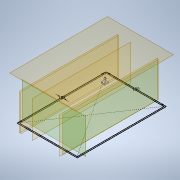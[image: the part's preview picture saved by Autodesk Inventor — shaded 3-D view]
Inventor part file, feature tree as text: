
AUTODESK INVENTOR PART (.ipt)
format: ipt  version: 2021 (Build 250183000, 183)  size: 425,984 bytes
history: native  units: in
note: dims shown in document units (in); Inventor stores cm internally (conversion verified against a paired STEP export)
features: sketch x26, extrude x20, reference x16, plane x7, mirror x4, other x4, revolve x2, chamfer x1, fillet x1
ambient origin geometry x8: Origin, YZ Plane, XZ Plane, XY Plane, X Axis, Y Axis, Z Axis, Center Point
bodies: Solid1 (feature_tree)
feature tree (81):
  sketch  "Sketch1"  dims[d0=3.937in d1=5.9055in]
  extrude  "Extrusion1"  Depth=5.9055in
  extrude  "Extrusion2"  Depth=0.0787in TaperAngle=0.0deg
  sketch  "Sketch2"  dims[d5=0.0787in d6=0.0in d7=-1.5748in]
  plane  "Work Plane1"
  extrude  "Extrusion3"  [1 undecoded]
  sketch  "Sketch7"  dims[d19=0.1181in d20=0.0in d21=2.8346in]
  plane  "Work Plane2"
  revolve  "Revolution2"  [1 undecoded]
  plane  "Work Plane3"
  extrude  "Extrusion4"  Depth=0.7087in
  sketch  "Sketch Driven Pattern1"  dims[d2=0.0787in d3=2.1654in d4=0.0in]
  extrude  "Extrusion5"  Depth=2.8346in
  plane  "Work Plane4"
  extrude  "Extrusion6"  Depth=0.1102in
  extrude  "Extrusion7"  Depth=0.1339in
  extrude  "Extrusion8"  TaperAngle=90.0deg  [1 undecoded]
  mirror  "Mirror1"
  plane  "Work Plane5"
  extrude  "Extrusion9"  Depth=0.0118in
  extrude  "Extrusion10"  Depth=0.0299in
  extrude  "Extrusion11"  Depth=0.0787in
  chamfer  "Chamfer1"  Distance=0.0787in
  extrude  "Extrusion12"  Depth=1.1811in
  sketch  "Sketch22"  dims[d47=0.5933in d48=0.0in d49=0.0866in]
  plane  "Work Plane6"
  revolve  "Revolution3"  [1 undecoded]
  extrude  "Extrusion13"  Depth=0.3819in
  sketch  "Sketch Driven Pattern2"  dims[d15=1.378in d16=1.2598in]
  extrude  "Extrusion14"  Depth=0.0866in
  extrude  "Extrusion15"  Depth=0.3236in
  extrude  "Extrusion16"  Depth=0.4724in
  plane  "Work Plane7"
  mirror  "Mirror2"
  extrude  "Extrusion17"  Depth=0.0787in TaperAngle=45.0deg
  extrude  "Extrusion18"  Depth=0.3937in
  extrude  "Extrusion19"  Depth=0.9843in
  mirror  "Mirror3"
  mirror  "Mirror4"
  fillet  "Fillet1"  Radius=0.5933in
  extrude  "Extrusion20"  Depth=0.4409in
  sketch  "Sketch6"  dims[d17=1.0236in d18=0.7087in]
  reference  "Reference1"
  reference  "Reference2"
  reference  "Reference3"
  reference  "Reference4"
  sketch  "Sketch8"  dims[d22=0.7087in d23=0.1102in]
  sketch  "Sketch9"  dims[d26=0.1063in d27=0.1339in]
  sketch  "Sketch10"  dims[d28=0.1929in d30=90.0deg]
  reference  "Reference5"
  reference  "Reference6"
  reference  "Reference7"
  reference  "Reference8"
  reference  "Reference9"
  reference  "Reference10"
  sketch  "Sketch11"  dims[d31=3.0in d32=0.0118in]
  sketch  "Sketch13"  dims[d33=0.1946in d34=0.0299in]
  sketch  "Sketch15"  dims[d35=0.0787in d36=0.0in d37=0.0157in]
  sketch  "Sketch18"  dims[d38=0.0157in d39=0.0787in d40=0.0in]
  sketch  "Sketch19"  dims[d41=0.9055in d42=1.1811in]
  sketch  "Sketch20"  dims[d43=0.4606in d44=0.9843in]
  sketch  "Sketch21"  dims[d45=0.0906in d46=0.3819in]
  reference  "Reference11"
  reference  "Reference12"
  reference  "Reference13"
  reference  "Reference14"
  reference  "Reference15"
  reference  "Reference16"
  sketch  "Sketch25"  dims[d50=0.4409in d51=0.3236in]
  sketch  "Sketch26"  dims[d52=0.5933in d53=0.0in d54=0.4724in]
  sketch  "Sketch27"  dims[d55=0.5933in d56=0.0in d57=0.1575in d58=0.0787in d59=45.0deg]
  sketch  "Sketch29"  dims[d63=0.3937in d64=0.0906in]
  sketch  "Sketch30"  dims[d65=0.4606in d66=0.9843in d67=0.5933in d68=0.0in]
  sketch  "Sketch31"  dims[d69=0.0866in d70=0.4409in]
  sketch  "Sketch34"  dims[d71=0.3236in]
  sketch  "Sketch35"  dims[d72=0.5933in d73=0.0in]
  sketch  "Sketch36"  dims[d74=0.4724in d75=0.5933in d76=0.0in d77=0.2756in d78=0.5906in d79=0.1181in d80=0.0in d81=90.0deg d82=0.0276in d83=0.0394in d84=0.0in d85=0.2362in d86=0.5906in d87=0.3937in d88=0.2697in d89=0.0in d90=0.1496in d91=0.0591in d92=0.0in d93=0.0906in d94=0.1969in d95=0.0in d96=0.689in d98=0.4724in d99=0.2362in d100=0.0in d101=0.2362in d102=0.2165in d103=0.2165in d104=0.0984in d105=0.0in d106=0.1299in d107=0.0in d108=0.0in d109=0.1969in d110=7.874in d111=0.0in]
  other  "Chestbox_with_electronical_devices.iam"
  other  "ArduinoMega_STEP_AP203:1"
  other  "TCA9548A Adfruit with Header:1"
  other  "Part57"
note: 4 required parameter values undecoded (feature->parameter linkage not recoverable at this tier; creation-order binding heuristic only, values carry confidence <= 0.55)